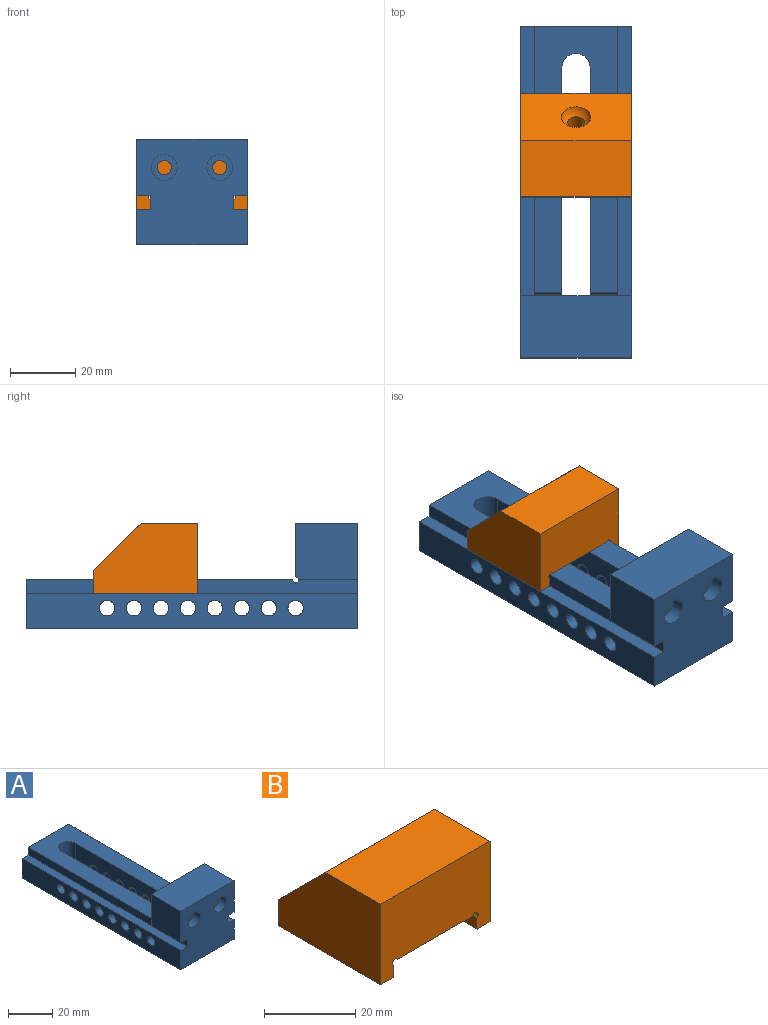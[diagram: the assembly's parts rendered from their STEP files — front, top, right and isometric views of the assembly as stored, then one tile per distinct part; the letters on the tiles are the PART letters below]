
ASSEMBLY  parts=2 mates=2
PART A: 71 faces, bbox 33.9x101.6x32.4 mm
  f0: cylinder r=2.38mm len=12.65mm, axis (1,0,0), area 162.1mm2, adj f31,f43,f45,f46,f61
  f1: cylinder r=2.38mm len=12.65mm, axis (1,0,0), area 162.1mm2, adj f31,f43,f46,f47,f61
  f2: cylinder r=2.38mm len=12.65mm, axis (1,0,0), area 162.1mm2, adj f31,f43,f47,f48,f61
  f3: cylinder r=2.38mm len=12.65mm, axis (1,0,0), area 162.1mm2, adj f31,f43,f48,f49,f61
  f4: cylinder r=2.38mm len=12.65mm, axis (1,0,0), area 162.1mm2, adj f31,f43,f49,f50,f61
  f5: cylinder r=2.38mm len=12.65mm, axis (1,0,0), area 162.1mm2, adj f31,f43,f50,f51,f61
  f6: cylinder r=2.38mm len=12.65mm, axis (1,0,0), area 162.1mm2, adj f31,f43,f51,f52,f61
  f7: cylinder r=2.38mm len=12.65mm, axis (1,0,0), area 162.1mm2, adj f31,f43,f52,f53,f61
  f8: cylinder r=2.38mm len=12.65mm, axis (1,0,0), area 162.1mm2, adj f32,f44,f45,f54,f63
  f9: cylinder r=2.38mm len=12.65mm, axis (1,0,0), area 162.1mm2, adj f32,f44,f54,f55,f63
  f10: cylinder r=2.38mm len=12.65mm, axis (1,0,0), area 162.1mm2, adj f32,f44,f55,f56,f63
  f11: cylinder r=2.38mm len=12.65mm, axis (1,0,0), area 162.1mm2, adj f32,f44,f56,f57,f63
  f12: cylinder r=2.38mm len=12.65mm, axis (1,0,0), area 162.1mm2, adj f32,f44,f57,f58,f63
  f13: cylinder r=2.38mm len=12.65mm, axis (1,0,0), area 162.1mm2, adj f32,f44,f58,f59,f63
  f14: cylinder r=2.38mm len=12.65mm, axis (1,0,0), area 162.1mm2, adj f32,f44,f59,f63,f64
  f15: cylinder r=2.38mm len=12.65mm, axis (1,0,0), area 162.1mm2, adj f32,f44,f53,f63,f64
  f16: cylinder r=4.3mm len=8.66mm, axis (0,0,-1), area 117mm2, adj f18,f43,f44,f45
  f17: cylinder r=4.3mm len=8.66mm, axis (0,0,-1), area 117mm2, adj f42,f43,f44,f53
  f18: plane 81.43x25.65mm, normal (0,0,1), area 1468.8mm2, adj f16,f21,f29,f34,f37,f39,f43,f44
  f19: plane 101.6x33.91mm, normal (0,0,-1), area 2087.9mm2, adj f31,f32,f36,f37,f60,f61,f62,f63
  f20: plane 8.53x0.58mm, normal (0,0.71,0.71), area 7mm2, adj f22,f23,f29,f43
  f21: plane 8.53x0.85mm, normal (0,-0.71,0.71), area 10.3mm2, adj f18,f23,f29,f43
  f22: cylinder r=0.38mm len=25.65mm, axis (-1,0,0), area 12.8mm2, adj f20,f29,f34,f38,f40,f42,f43,f44
  f23: cylinder r=0.38mm len=8.53mm, axis (1,0,0), area 5.1mm2, adj f20,f21,f29,f43
  f24: plane 19.05x17.37mm, normal (-1,0,0), area 330.3mm2, adj f26,f27,f28,f36,f40
  f25: plane 19.05x17.37mm, normal (1,0,0), area 330.3mm2, adj f26,f27,f35,f36,f40
  f26: plane 33.91x16.25mm, normal (0,1,0), area 521.9mm2, adj f24,f25,f27,f40,f65,f68
  f27: plane 33.91x19.05mm, normal (0,0,1), area 646mm2, adj f24,f25,f26,f36
  f28: plane 17.93x4.13mm, normal (0,0,-1), area 74mm2, adj f24,f29,f36,f40
  f29: plane 101.6x4.49mm, normal (-1,0,0), area 427.2mm2, adj f18,f20,f21,f22,f23,f28,f30,f36
  f30: plane 101.6x4.13mm, normal (0,0,1), area 419.4mm2, adj f29,f31,f36,f37
  f31: plane 101.6x10.8mm, normal (-1,0,0), area 954.3mm2, adj f0,f1,f2,f3,f4,f5,f6,f7
  f32: plane 101.6x10.8mm, normal (1,0,0), area 954.3mm2, adj f8,f9,f10,f11,f12,f13,f14,f15
  f33: plane 101.6x4.13mm, normal (0,0,1), area 419.4mm2, adj f32,f34,f36,f37
  f34: plane 101.6x4.49mm, normal (1,0,0), area 427.2mm2, adj f18,f22,f33,f35,f36,f37,f38,f39
  f35: plane 17.93x4.13mm, normal (0,0,-1), area 74mm2, adj f25,f34,f36,f40
  f36: plane 33.91x32.39mm, normal (0,-1,0), area 964.4mm2, adj f19,f24,f25,f27,f28,f29,f30,f31
  f37: plane 33.91x15.01mm, normal (0,1,0), area 474.2mm2, adj f18,f19,f29,f30,f31,f32,f33,f34
  f38: plane 8.53x0.58mm, normal (0,0.71,0.71), area 7mm2, adj f22,f34,f41,f44
  f39: plane 8.53x0.85mm, normal (0,-0.71,0.71), area 10.3mm2, adj f18,f34,f41,f44
  f40: plane 33.91x1.12mm, normal (0,0.71,-0.71), area 44.1mm2, adj f22,f24,f25,f26,f28,f29,f34,f35
  f41: cylinder r=0.38mm len=8.53mm, axis (1,0,0), area 5.1mm2, adj f34,f38,f39,f44
  f42: plane 8.6x6.51mm, normal (0,0,-1), area 48.1mm2, adj f17,f22,f43,f44
  f43: plane 73.03x8.66mm, normal (1,0,0), area 560mm2, adj f0,f1,f2,f3,f4,f5,f6,f7
  f44: plane 73.03x8.66mm, normal (-1,0,0), area 560mm2, adj f8,f9,f10,f11,f12,f13,f14,f15
  f45: plane 17.62x15.88mm, normal (0,0,-1), area 140.4mm2, adj f0,f8,f16,f43,f44,f61,f62,f63
  f46: plane 3.64x3.49mm, normal (0,0,-1), area 12.7mm2, adj f0,f1,f43,f61
  f47: plane 3.64x3.49mm, normal (0,0,-1), area 12.7mm2, adj f1,f2,f43,f61
  f48: plane 3.64x3.49mm, normal (0,0,-1), area 12.7mm2, adj f2,f3,f43,f61
  f49: plane 3.64x3.49mm, normal (0,0,-1), area 12.7mm2, adj f3,f4,f43,f61
  f50: plane 3.64x3.49mm, normal (0,0,-1), area 12.7mm2, adj f4,f5,f43,f61
  f51: plane 3.64x3.49mm, normal (0,0,-1), area 12.7mm2, adj f5,f6,f43,f61
  f52: plane 3.64x3.49mm, normal (0,0,-1), area 12.7mm2, adj f6,f7,f43,f61
  f53: plane 15.88x8.73mm, normal (0,0,-1), area 75.7mm2, adj f7,f15,f17,f43,f44,f60,f61,f63
  f54: plane 3.64x3.49mm, normal (0,0,-1), area 12.7mm2, adj f8,f9,f44,f63
  f55: plane 3.64x3.49mm, normal (0,0,-1), area 12.7mm2, adj f9,f10,f44,f63
  f56: plane 3.64x3.49mm, normal (0,0,-1), area 12.7mm2, adj f10,f11,f44,f63
  f57: plane 3.64x3.49mm, normal (0,0,-1), area 12.7mm2, adj f11,f12,f44,f63
  f58: plane 3.64x3.49mm, normal (0,0,-1), area 12.7mm2, adj f12,f13,f44,f63
  f59: plane 3.64x3.49mm, normal (0,0,-1), area 12.7mm2, adj f13,f14,f44,f63
  f60: cylinder r=7.94mm len=15.88mm, axis (0,0,-1), area 158.3mm2, adj f19,f53,f61,f63
  f61: plane 73.03x6.35mm, normal (1,0,0), area 392.5mm2, adj f0,f1,f2,f3,f4,f5,f6,f7
  f62: cylinder r=7.94mm len=15.88mm, axis (0,0,-1), area 158.3mm2, adj f19,f45,f61,f63
  f63: plane 73.03x6.35mm, normal (-1,0,0), area 392.5mm2, adj f8,f9,f10,f11,f12,f13,f14,f15
  f64: plane 3.64x3.49mm, normal (0,0,-1), area 12.7mm2, adj f14,f15,f44,f63
  f65: cylinder r=2.15mm len=14.88mm, axis (0,-1,0), area 201.3mm2, adj f26,f66
  f66: plane 7.94x7.94mm, normal (0,-1,0), area 34.9mm2, adj f65,f67
  f67: cylinder r=3.97mm len=7.94mm, axis (0,-1,0), area 103.9mm2, adj f36,f66
  f68: cylinder r=2.15mm len=14.88mm, axis (0,-1,0), area 201.3mm2, adj f26,f69
  f69: plane 7.94x7.94mm, normal (0,-1,0), area 34.9mm2, adj f68,f70
  f70: cylinder r=3.97mm len=7.94mm, axis (0,-1,0), area 103.9mm2, adj f36,f69
PART B: 25 faces, bbox 33.9x31.8x21.6 mm
  f0: cylinder r=2.58mm len=13.84mm, axis (0,0.71,0.71), area 191.6mm2, adj f2,f22
  f1: plane 31.75x2.94mm, normal (-1,0,0), area 93.4mm2, adj f4,f5,f13,f24
  f2: plane 31.75x23.42mm, normal (0,0,-1), area 714.1mm2, adj f0,f4,f5,f12,f15
  f3: plane 31.75x2.94mm, normal (1,0,0), area 93.4mm2, adj f4,f5,f17,f23
  f4: plane 33.91x6.96mm, normal (0,1,0), area 126.9mm2, adj f1,f2,f3,f6,f8,f9,f10,f11
  f5: plane 33.91x21.56mm, normal (0,-1,0), area 622.1mm2, adj f1,f2,f3,f6,f7,f8,f9,f10
  f6: plane 31.75x21.56mm, normal (1,0,0), area 578mm2, adj f4,f5,f7,f8,f11
  f7: plane 33.91x17.15mm, normal (0,0,1), area 581.4mm2, adj f5,f6,f10,f11
  f8: plane 31.75x3.99mm, normal (0,0,-1), area 126.8mm2, adj f4,f5,f6,f24
  f9: plane 31.75x3.99mm, normal (0,0,-1), area 126.8mm2, adj f4,f5,f10,f23
  f10: plane 31.75x21.56mm, normal (-1,0,0), area 578mm2, adj f4,f5,f7,f9,f11
  f11: plane 33.91x14.61mm, normal (0,0.71,0.71), area 637mm2, adj f4,f6,f7,f10,f22
  f12: plane 31.75x0.38mm, normal (0.71,0,-0.71), area 17.1mm2, adj f2,f4,f5,f19
  f13: plane 31.75x0.38mm, normal (-0.71,0,0.71), area 17.1mm2, adj f1,f4,f5,f18
  f14: plane 31.75x0.58mm, normal (-0.71,0,-0.71), area 26.2mm2, adj f4,f5,f18,f19
  f15: plane 31.75x0.38mm, normal (-0.71,0,-0.71), area 17.1mm2, adj f2,f4,f5,f21
  f16: plane 31.75x0.58mm, normal (0.71,0,-0.71), area 26.2mm2, adj f4,f5,f20,f21
  f17: plane 31.75x0.38mm, normal (0.71,0,0.71), area 17.1mm2, adj f3,f4,f5,f20
  f18: cylinder r=0.38mm len=31.75mm, axis (0,1,0), area 19mm2, adj f4,f5,f13,f14
  f19: cylinder r=0.38mm len=31.75mm, axis (0,-1,0), area 19mm2, adj f4,f5,f12,f14
  f20: cylinder r=0.38mm len=31.75mm, axis (0,-1,0), area 19mm2, adj f4,f5,f16,f17
  f21: cylinder r=0.38mm len=31.75mm, axis (0,1,0), area 19mm2, adj f4,f5,f15,f16
  f22: sphere r=4.76mm, area 72.3mm2, adj f0,f11
  f23: plane 31.75x0.13mm, normal (0.71,0,-0.71), area 5.7mm2, adj f3,f4,f5,f9
  f24: plane 31.75x0.13mm, normal (-0.71,0,-0.71), area 5.7mm2, adj f1,f4,f5,f8
PLACE A t=(83.11,-51.74,0.07)mm
PLACE B t=(83.12,-21.55,0.07)mm
MATE planar A.f18 <-> B.f2  axis (0,0,1) through (83.11,49.86,-1.12)mm
MATE planar B.f3 <-> A.f29  axis (1,0,0) through (70.28,29.25,-3.71)mm
